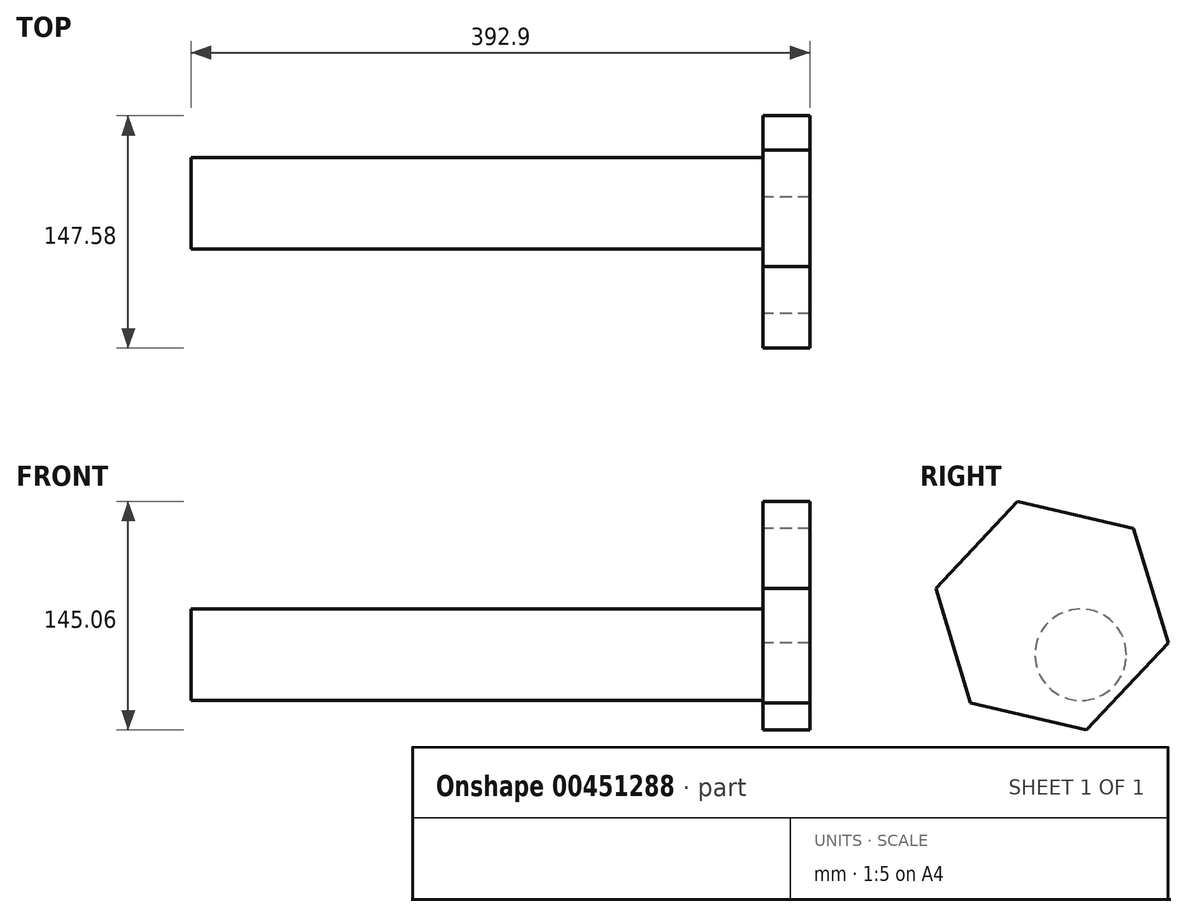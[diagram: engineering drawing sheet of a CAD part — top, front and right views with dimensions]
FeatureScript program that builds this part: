
annotation { "Feature Type Name" : "Feature", "Feature Type Description" : "" }
export const myFeature = defineFeature(function(context is Context, id is Id, definition is map)
    precondition{}
    {
        {
            var Q0;
            Q0=qCreatedBy(makeId("Right.planeOp"),FACE);
            var sketch = newSketch(context, id + "F0", { "sketchPlane" : qUnion([Q0])});
            skCircle(sketch, "E0.cCircle", {"center": v(0, 0) * mm, "radius": 75.78 * mm, "construction": true});
            skLineSegment(sketch, "E0.0", {"start": v(-51.83, -55.28) * mm, "end": v(-73.8, 17.25) * mm});
            skLineSegment(sketch, "E0.1", {"start": v(-73.8, 17.25) * mm, "end": v(-21.96, 72.53) * mm});
            skLineSegment(sketch, "E0.2", {"start": v(-21.96, 72.53) * mm, "end": v(51.83, 55.28) * mm});
            skLineSegment(sketch, "E0.3", {"start": v(51.83, 55.28) * mm, "end": v(73.8, -17.25) * mm});
            skLineSegment(sketch, "E0.4", {"start": v(73.8, -17.25) * mm, "end": v(21.96, -72.53) * mm});
            skLineSegment(sketch, "E0.5", {"start": v(21.96, -72.53) * mm, "end": v(-51.83, -55.28) * mm});
            skSolve(sketch);
        }
        {
            var Q0;
            Q0 = qSketchRegion(id + "F0", true);
            extrude(context, id + "F1", {"entities" : qUnion([Q0]), "depth" : 29.8 * mm});
        }
        {
            var Q0;
            Q0=qCreatedBy(makeId("Right.planeOp"),FACE);
            var sketch = newSketch(context, id + "F2", { "sketchPlane" : qUnion([Q0])});
            skCircle(sketch, "E1", {"center": v(18.2, -24.82) * mm, "radius": 29.03 * mm});
            skSolve(sketch);
        }
        {
            var Q0;
            Q0 = qSketchRegion(id + "F2", true);
            extrude(context, id + "F3", {"entities" : qUnion([Q0]), "operationType" : NewBodyOperationType.ADD, "oppositeDirection" : true, "depth" : 71 * mm});
        }
        {
            var Q0;
            Q0=makeQuery(id+"F3.opExtrude","CAP_FACE",FACE,{"disambiguationData":[OSD([sQuery(id+"F2.wireOp",EDGE,"E1")])],"isStart":false});
            extrude(context, id + "F4", {"entities" : qUnion([Q0]), "operationType" : NewBodyOperationType.ADD, "depth" : 292.08 * mm});
        }
    });
